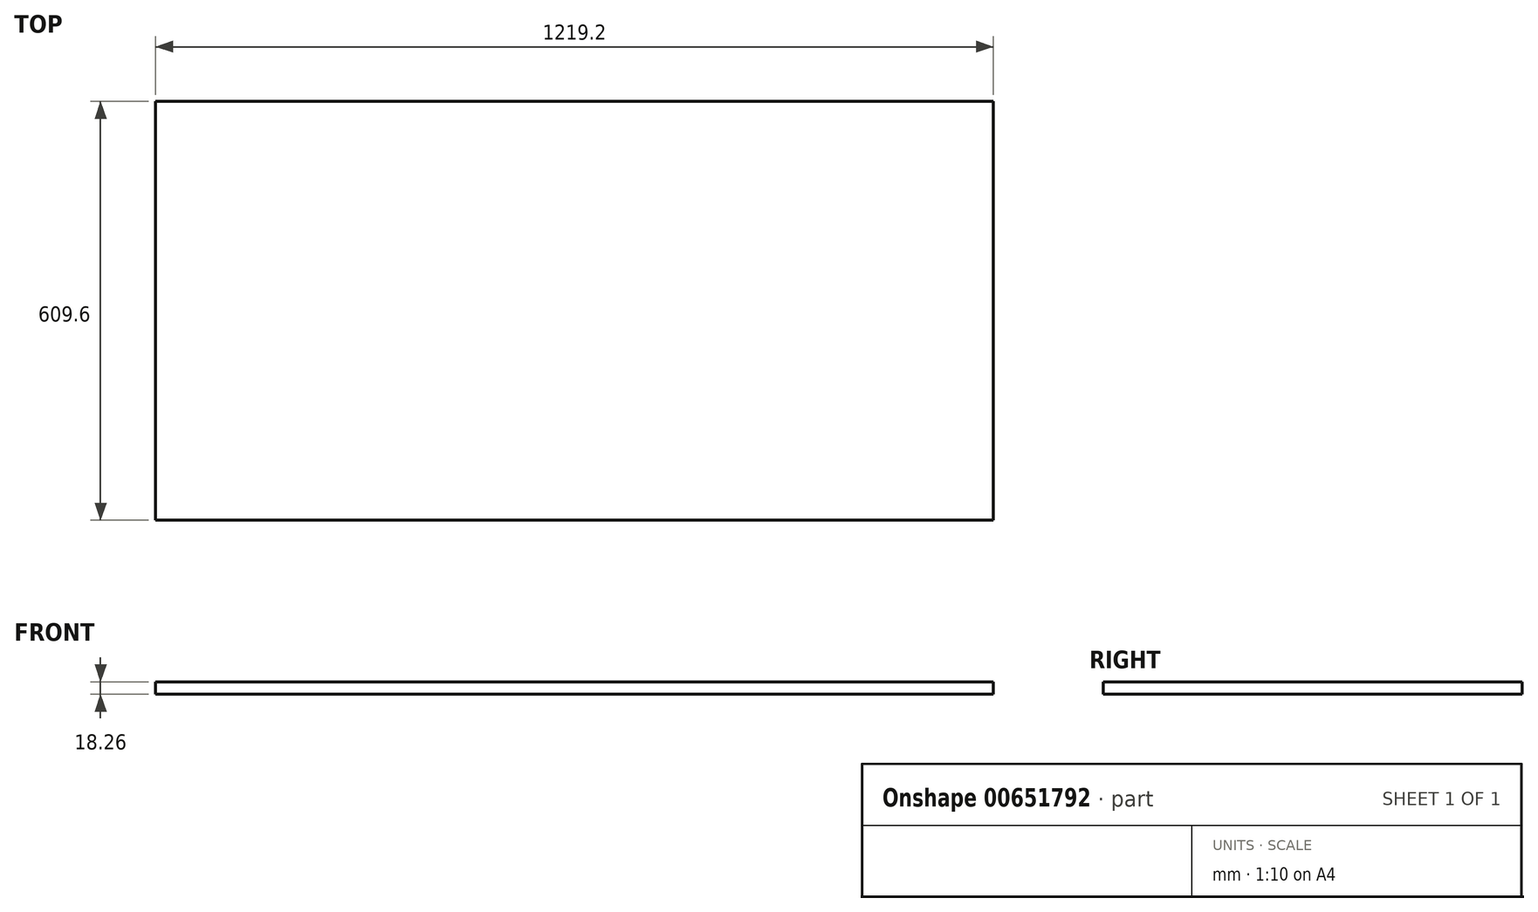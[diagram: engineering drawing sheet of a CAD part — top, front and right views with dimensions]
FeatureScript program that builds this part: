
annotation { "Feature Type Name" : "Feature", "Feature Type Description" : "" }
export const myFeature = defineFeature(function(context is Context, id is Id, definition is map)
    precondition{}
    {
        {
            var Q0;
            Q0=qCreatedBy(makeId("Top.planeOp"),FACE);
            var sketch = newSketch(context, id + "F0", { "sketchPlane" : qUnion([Q0])});
            skLineSegment(sketch, "E0.bottom", {"start": v(0, 0) * mm, "end": v(1219.2, 0) * mm});
            skLineSegment(sketch, "E0.top", {"start": v(0, 609.6) * mm, "end": v(1219.2, 609.6) * mm});
            skLineSegment(sketch, "E0.left", {"start": v(0, 0) * mm, "end": v(0, 609.6) * mm});
            skLineSegment(sketch, "E0.right", {"start": v(1219.2, 0) * mm, "end": v(1219.2, 609.6) * mm});
            skSolve(sketch);
        }
        {
            var Q0;
            Q0=makeQuery(id+"F0.imprint","IMPRINT",FACE,{"disambiguationData":[TD([[makeQuery(id+"F0.imprint","IMPRINT",EDGE,{"derivedFrom":sQuery(id+"F0.wireOp",EDGE,"E0.bottom")}),1.0]])]});
            extrude(context, id + "F1", {"entities" : qUnion([Q0]), "depth" : 18.26 * mm, "offsetDistance" : 25.4 * mm});
        }
    });
